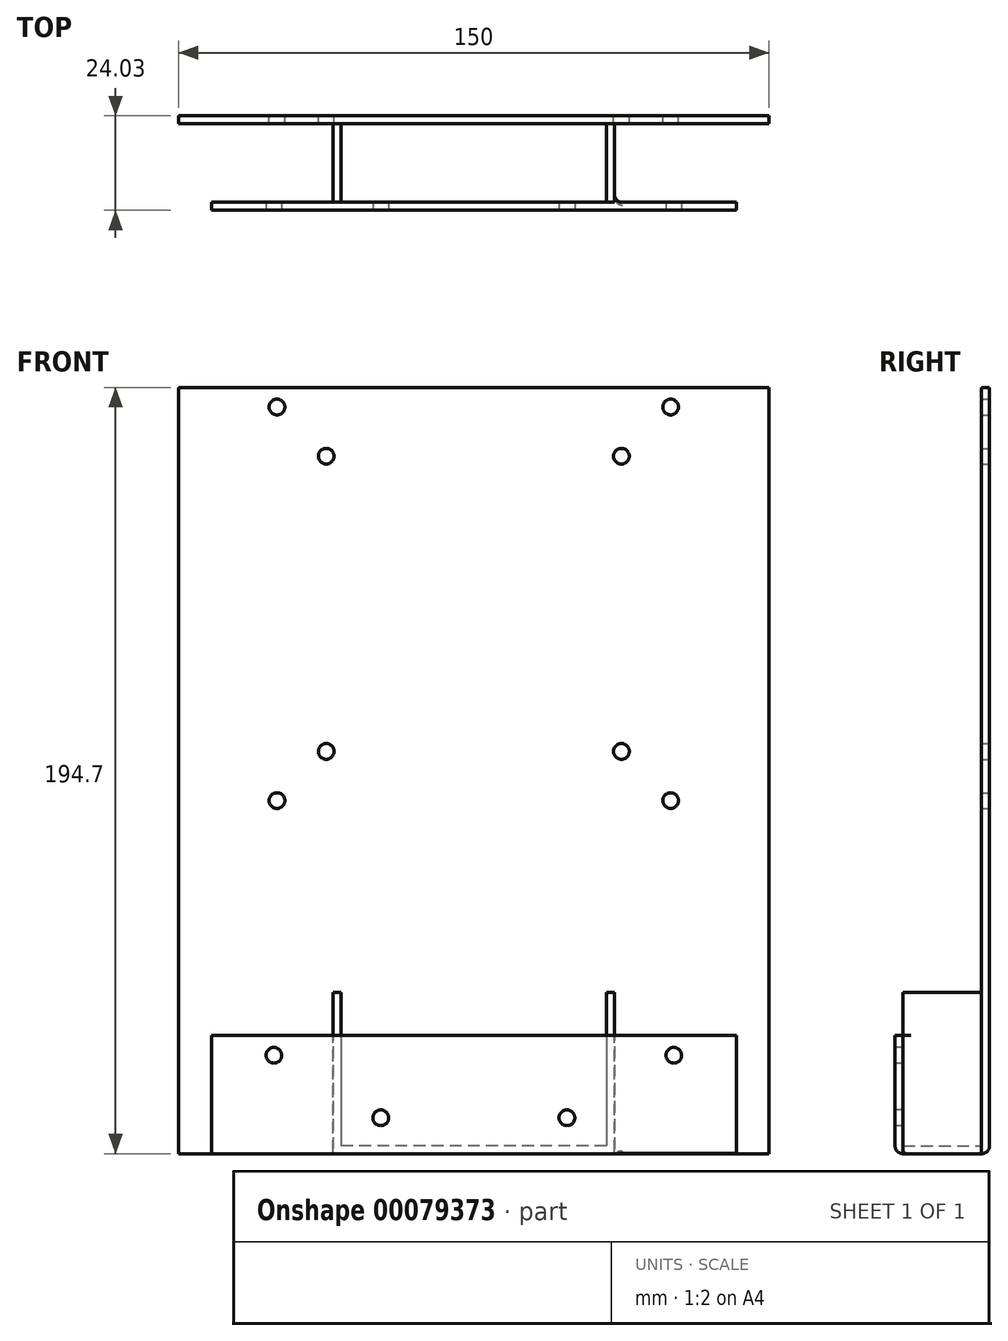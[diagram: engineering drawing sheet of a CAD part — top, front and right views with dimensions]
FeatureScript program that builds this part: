
annotation { "Feature Type Name" : "Feature", "Feature Type Description" : "" }
export const myFeature = defineFeature(function(context is Context, id is Id, definition is map)
    precondition{}
    {
        {
            var Q0;
            Q0=qCreatedBy(makeId("Front.planeOp"),FACE);
            var sketch = newSketch(context, id + "F0", { "sketchPlane" : qUnion([Q0])});
            skCircle(sketch, "E0", {"center": v(-37.5, 37.5) * mm, "radius": 2 * mm});
            skCircle(sketch, "E1", {"center": v(37.5, 37.5) * mm, "radius": 2 * mm});
            skCircle(sketch, "E2", {"center": v(-37.5, -37.5) * mm, "radius": 2 * mm});
            skCircle(sketch, "E3", {"center": v(37.5, -37.5) * mm, "radius": 2 * mm});
            skCircle(sketch, "E4", {"center": v(-50, 50) * mm, "radius": 2 * mm});
            skCircle(sketch, "E5", {"center": v(50, 50) * mm, "radius": 2 * mm});
            skCircle(sketch, "E6", {"center": v(50, -50) * mm, "radius": 2 * mm});
            skCircle(sketch, "E7", {"center": v(-50, -50) * mm, "radius": 2 * mm});
            skLineSegment(sketch, "E8.bottom", {"start": v(-75, 55) * mm, "end": v(75, 55) * mm});
            skLineSegment(sketch, "E8.left", {"start": v(-75, 55) * mm, "end": v(-75, -139.7) * mm});
            skLineSegment(sketch, "E8.right", {"start": v(75, 55) * mm, "end": v(75, -139.7) * mm});
            skPoint(sketch, "E8.middle", {"position": v(0, 0) * mm});
            skLineSegment(sketch, "E9", {"start": v(75, -139.7) * mm, "end": v(-75, -139.7) * mm});
            skSolve(sketch);
        }
        {
            var Q0;
            Q0=makeQuery(id+"F0.imprint","IMPRINT",FACE,{"disambiguationData":[TD([[makeQuery(id+"F0.imprint","IMPRINT",EDGE,{"derivedFrom":sQuery(id+"F0.wireOp",EDGE,"E0")}),-1.0]])]});
            extrude(context, id + "F1", {"entities" : qUnion([Q0]), "depth" : 2.03 * mm});
        }
        {
            var Q0;
            Q0=qCreatedBy(makeId("Right.planeOp"),FACE);
            var sketch = newSketch(context, id + "F2", { "sketchPlane" : qUnion([Q0])});
            skLineSegment(sketch, "E10", {"start": v(-22.03, -139.7) * mm, "end": v(-24.03, -139.7) * mm});
            skLineSegment(sketch, "E11", {"start": v(-24.03, -139.7) * mm, "end": v(-24.03, -109.7) * mm});
            skLineSegment(sketch, "E12.0", {"start": v(-22.03, -139.7) * mm, "end": v(-22.03, -109.7) * mm});
            skLineSegment(sketch, "E13", {"start": v(-24.03, -109.7) * mm, "end": v(-22.03, -109.7) * mm});
            skLineSegment(sketch, "E14.0", {"start": v(-22.03, -139.7) * mm, "end": v(-2.03, -139.7) * mm});
            skLineSegment(sketch, "E15", {"start": v(-22.03, -139.7) * mm, "end": v(-22.03, -137.7) * mm, "construction": true});
            skLineSegment(sketch, "E16", {"start": v(-22.03, -137.7) * mm, "end": v(-2.03, -137.7) * mm});
            skLineSegment(sketch, "E17", {"start": v(-2.03, -137.7) * mm, "end": v(-2.03, -139.7) * mm});
            skSolve(sketch);
        }
        {
            var Q0;
            {var subQ0=sQuery(id+"F2.wireOp",EDGE,"E14.0");Q0=makeQuery(id+"F2.imprint","IMPRINT",FACE,{"disambiguationData":[TD([[makeQuery(id+"F2.imprint","IMPRINT",EDGE,{"derivedFrom":subQ0}),1.0]])]});}
            var Q1;
            Q1=makeQuery(id+"F1.opExtrude","SWEPT_FACE",FACE,{"disambiguationData":[OSD([sQuery(id+"F0.wireOp",EDGE,"E8.right")])]});
            var Q2;
            Q2=makeQuery(id+"F1.opExtrude","SWEPT_FACE",FACE,{"disambiguationData":[OSD([sQuery(id+"F0.wireOp",EDGE,"E8.left")])]});
            extrude(context, id + "F3", {"entities" : qUnion([Q0]), "operationType" : NewBodyOperationType.ADD, "endBound" : BoundingType.SYMMETRIC, "endBoundEntityFace" : qUnion([Q1]), "depth" : 71.44 * mm, "hasSecondDirection" : true, "secondDirectionBound" : SecondDirectionBoundingType.UP_TO_SURFACE, "secondDirectionOppositeDirection" : true, "secondDirectionBoundEntityFace" : qUnion([Q2]), "secondDirectionDepth" : 80 * mm});
        }
        {
            var Q0;
            {var subQ3=sQuery(id+"F2.wireOp",EDGE,"E10");Q0=makeQuery(id+"F2.imprint","IMPRINT",FACE,{"disambiguationData":[TD([[makeQuery(id+"F2.imprint","IMPRINT",EDGE,{"derivedFrom":subQ3}),-1.0]])]});}
            extrude(context, id + "F4", {"entities" : qUnion([Q0]), "operationType" : NewBodyOperationType.ADD, "endBound" : BoundingType.SYMMETRIC, "depth" : 133.35 * mm});
        }
        {
            var Q0;
            Q0=makeQuery(id+"F4.opExtrude","SWEPT_FACE",FACE,{"disambiguationData":[OSD([sQuery(id+"F2.wireOp",EDGE,"E11")])]});
            var sketch = newSketch(context, id + "F5", { "sketchPlane" : qUnion([Q0])});
            skCircle(sketch, "E18", {"center": v(-50.8, -114.7) * mm, "radius": 2 * mm});
            skCircle(sketch, "E19", {"center": v(-23.65, -130.57) * mm, "radius": 2 * mm});
            skCircle(sketch, "E20.MirrorC", {"center": v(50.8, -114.7) * mm, "radius": 2 * mm});
            skCircle(sketch, "E21.MirrorC", {"center": v(23.65, -130.57) * mm, "radius": 2 * mm});
            skSolve(sketch);
        }
        {
            var Q0;
            Q0 = qSketchRegion(id + "F5", true);
            extrude(context, id + "F6", {"entities" : qUnion([Q0]), "operationType" : NewBodyOperationType.REMOVE, "endBound" : BoundingType.UP_TO_NEXT, "oppositeDirection" : true, "depth" : 25 * mm});
        }
        {
            var Q0;
            Q0=makeQuery(id+"F3.opExtrude","SWEPT_FACE",FACE,{"disambiguationData":[OSD([sQuery(id+"F2.wireOp",EDGE,"E16")])]});
            var sketch = newSketch(context, id + "F7", { "sketchPlane" : qUnion([Q0])});
            skLineSegment(sketch, "E22.bottom", {"start": v(-35.72, -2.03) * mm, "end": v(-33.69, -2.03) * mm});
            skLineSegment(sketch, "E22.top", {"start": v(-35.72, -22.03) * mm, "end": v(-33.69, -22.03) * mm});
            skLineSegment(sketch, "E22.left", {"start": v(-35.72, -2.03) * mm, "end": v(-35.72, -22.03) * mm});
            skLineSegment(sketch, "E22.right", {"start": v(-33.69, -2.03) * mm, "end": v(-33.69, -22.03) * mm});
            skLineSegment(sketch, "E23.bottom", {"start": v(35.72, -22.03) * mm, "end": v(33.69, -22.03) * mm});
            skLineSegment(sketch, "E23.top", {"start": v(35.72, -2.03) * mm, "end": v(33.69, -2.03) * mm});
            skLineSegment(sketch, "E23.left", {"start": v(35.72, -22.03) * mm, "end": v(35.72, -2.03) * mm});
            skLineSegment(sketch, "E23.right", {"start": v(33.69, -22.03) * mm, "end": v(33.69, -2.03) * mm});
            skSolve(sketch);
        }
        {
            var Q0;
            Q0 = qSketchRegion(id + "F7", true);
            extrude(context, id + "F8", {"entities" : qUnion([Q0]), "operationType" : NewBodyOperationType.ADD, "depth" : 39 * mm});
        }
        {
            var Q0;
            Q0=makeQuery(id+"F8.boolean.opBoolean","MERGE",EDGE,{"derivedFrom":[makeQuery(id+"F3.opExtrude","CAP_EDGE",EDGE,{"disambiguationData":[OSD([sQuery(id+"F2.wireOp",EDGE,"E17")])],"isStart":false}),makeQuery(id+"F8.opExtrude","SWEPT_EDGE",EDGE,{"disambiguationData":[OSD([sQuery(id+"F7.wireOp",EDGE,"E23.top"),sQuery(id+"F7.wireOp",EDGE,"E23.left")])]})]});
            var Q1;
            Q1=makeQuery(id+"F8.boolean.opBoolean","MERGE",EDGE,{"derivedFrom":[makeQuery(id+"F3.opExtrude","CAP_EDGE",EDGE,{"disambiguationData":[OSD([sQuery(id+"F2.wireOp",EDGE,"E12.0")])],"isStart":false}),makeQuery(id+"F8.opExtrude","SWEPT_EDGE",EDGE,{"disambiguationData":[OSD([sQuery(id+"F7.wireOp",EDGE,"E23.bottom"),sQuery(id+"F7.wireOp",EDGE,"E23.left")])]})]});
            var Q2;
            Q2=makeQuery(id+"F8.boolean.opBoolean","MERGE",EDGE,{"derivedFrom":[makeQuery(id+"F3.opExtrude","CAP_EDGE",EDGE,{"disambiguationData":[OSD([sQuery(id+"F2.wireOp",EDGE,"E17")])],"isStart":true}),makeQuery(id+"F8.opExtrude","SWEPT_EDGE",EDGE,{"disambiguationData":[OSD([sQuery(id+"F7.wireOp",EDGE,"E22.bottom"),sQuery(id+"F7.wireOp",EDGE,"E22.left")])]})]});
            var Q3;
            Q3=makeQuery(id+"F8.boolean.opBoolean","MERGE",EDGE,{"derivedFrom":[makeQuery(id+"F3.opExtrude","CAP_EDGE",EDGE,{"disambiguationData":[OSD([sQuery(id+"F2.wireOp",EDGE,"E12.0")])],"isStart":true}),makeQuery(id+"F8.opExtrude","SWEPT_EDGE",EDGE,{"disambiguationData":[OSD([sQuery(id+"F7.wireOp",EDGE,"E22.top"),sQuery(id+"F7.wireOp",EDGE,"E22.left")])]})]});
            fillet(context, id + "F9", {"entities" : qUnion([Q0, Q1, Q2, Q3]), "radius" : 2 * mm, "tangentPropagation" : true, "allowEdgeOverflow" : false});
        }
        {
            var Q0;
            Q0=makeQuery(id+"F1.opExtrude","CAP_EDGE",EDGE,{"disambiguationData":[OSD([sQuery(id+"F0.wireOp",EDGE,"E9")])],"isStart":true});
            var Q1;
            Q1=makeQuery(id+"F4.opExtrude","SWEPT_EDGE",EDGE,{"disambiguationData":[OSD([sQuery(id+"F2.wireOp",EDGE,"E10"),sQuery(id+"F2.wireOp",EDGE,"E11")])]});
            fillet(context, id + "F10", {"entities" : qUnion([Q0, Q1]), "radius" : 2 * mm, "allowEdgeOverflow" : false});
        }
        {
            var Q0;
            Q0=makeQuery(id+"F3.opExtrude","CAP_EDGE",EDGE,{"disambiguationData":[OSD([sQuery(id+"F2.wireOp",EDGE,"E14.0")])],"isStart":true});
            var Q1;
            Q1=makeQuery(id+"F3.opExtrude","CAP_EDGE",EDGE,{"disambiguationData":[OSD([sQuery(id+"F2.wireOp",EDGE,"E14.0")])],"isStart":false});
            var Q2;
            Q2=makeQuery(id+"F8.opExtrude","CAP_EDGE",EDGE,{"disambiguationData":[OSD([sQuery(id+"F7.wireOp",EDGE,"E23.right")])],"isStart":true});
            var Q3;
            Q3=makeQuery(id+"F8.opExtrude","CAP_EDGE",EDGE,{"disambiguationData":[OSD([sQuery(id+"F7.wireOp",EDGE,"E22.right")])],"isStart":true});
            fillet(context, id + "F11", {"entities" : qUnion([Q0, Q1, Q2, Q3]), "radius" : .5 * mm, "tangentPropagation" : true, "allowEdgeOverflow" : false});
        }
    });
